# Revit family: RN 12075 Redfil
name_source: partatom
category: Rohrzubehör
units: mm (PartAtom-declared; Revit-internal decimal feet)

## family parameters
Arbeitsebenenbasiert = Nein
Beim Laden mit Abzugskörper schneiden = Nein
Bemaßung runder Anschluss = Durchmesser verwenden
Gemeinsam genutzt = Nein
Immer vertikal = Ja
Teiletyp = Ventil - Zerlegung in

## types (4) — shared parameters
1.010.00.2 Blattnummer der Richtlinie = 17
1.010.00.3 Ausgabedatum (Monat) der Richtlinie = 201601
1.010.00.4 Herstellername = R. Nussbaum AG
1.010.00.5 Revisionsdatum der Datei = 20190528
1.010.00.6 Webadresse des Herstellers = http://www.nussbaum.ch
1.100.00.3 Sortiernummer für Anzeigereihenfolge = 9
1.100.00.4 Produktbezeichnung = Filterkombination, Filter und Schmutzfänger
1.960/3L.00.8 Link (URL) = https://www.nussbaum.ch
17.700.00.4 Armaturentyp = 8
17.700.00.7 Maximale Betriebstemperatur TB [°C] = 30
17.700.00.8 Maximaler Betriebsdruck (Arbeitsdruck) ps [1.0 · 105 Pa] = 16
Connector Visibility = Nein
EnclosingSpace Visibility = Nein
Hersteller = R. Nussbauzm AG
URL = https://www.nussbaum.ch

## per-type parameters (varying)
| type | 1.800.00.3 TGA-Nummer | 1.810.00.3 Hersteller-Bestellnummer | 1.810.00.4 DATANORM-Nummer | 1.810.00.6 GTIN-Nummer | 17.700.00.30 Produktbeschreibung | 17.700.00.5 Nennweite DN | 17.700.00.6 kvs-Wert [m3/h] | CONNECTOR0_DIAMETER_dY_0r | CONNECTOR0_dY_00 | CONNECTOR0_dY_01 | CONNECTOR0_ref_dX | CONNECTOR0_ref_dY | CONNECTOR1_DIAMETER_dY_0r | CONNECTOR1_dY_00 | CONNECTOR1_dY_01 | CONNECTOR1_ref_dX | CONNECTOR1_ref_dY | Modell | R. Nussbaum AG 12075.36 de Visibility | R. Nussbaum AG 12075.37 de Visibility | R. Nussbaum AG 12075.38 de Visibility | R. Nussbaum AG 12075.39 de Visibility | Typenkommentare |
| DN 25 | 00901200000000000000000000000200700000000000000001???00000 | 12075.36 | 12075.36 | 7612945817891 | 12075.36, Redfil, ohne Verschraubungen, mit Flansch 12085, DN=25 | 25 | 6 | 25 mm  [stored 0.082021 ft] | 50 mm | 39 mm | 102 mm | 50 mm | 25 mm  [stored 0.082021 ft] | 39 mm | 50 mm | 102 mm | 50 mm | 12075.36 | Ja | Nein | Nein | Nein | RedfilDN 25 |
| DN 32 | 00901200000000000000000000000200700000000000000002???00000 | 12075.37 | 12075.37 | 7612945817907 | 12075.37, Redfil, ohne Verschraubungen, mit Flansch 12085, DN=32 | 32 | 12 | 32 mm  [stored 0.104987 ft] | 60 mm | 46 mm | 102 mm | 60 mm | 32 mm  [stored 0.104987 ft] | 46 mm | 60 mm | 102 mm | 60 mm | 12075.37 | Nein | Ja | Nein | Nein | RedfilDN 32 |
| DN 40 | 00901200000000000000000000000200700000000000000003???00000 | 12075.38 | 12075.38 | 7612945817914 | 12075.38, Redfil, ohne Verschraubungen, mit Flansch 12085, DN=40 | 40 | 13.8 | 40 mm | 73 mm | 59 mm | 127 mm | 73 mm | 40 mm | 59 mm | 73 mm | 152 mm | 73 mm | 12075.38 | Nein | Nein | Ja | Nein | RedfilDN 40 |
| DN 50 | 00901200000000000000000000000200700000000000000004???00000 | 12075.39 | 12075.39 | 7612945817921 | 12075.39, Redfil, ohne Verschraubungen, mit Flansch 12085, DN=50 | 50 | 18 | 50 mm | 88 mm | 68 mm | 127 mm | 88 mm | 50 mm | 68 mm | 88 mm | 127 mm | 88 mm | 12075.39 | Nein | Nein | Nein | Ja | RedfilDN 50 |

note: [stored X ft] marks values corroborated as IEEE doubles in the binary element streams (Revit-internal decimal feet)

## geometry (parser evidence)
native form markers: Sweep x1
no freeform markers — native parametric forms only
